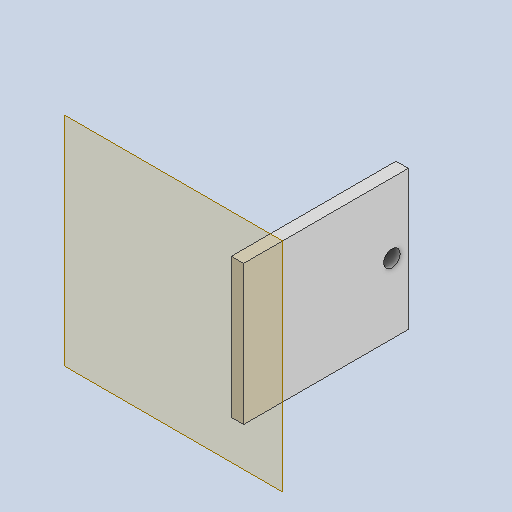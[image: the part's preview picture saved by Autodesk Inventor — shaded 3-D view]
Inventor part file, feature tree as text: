
AUTODESK INVENTOR PART (.ipt)
format: ipt  version: 2022.2 (Build 262287000, 287)  size: 88,576 bytes
history: native  units: in
note: dims shown in document units (in); Inventor stores cm internally (conversion verified against a paired STEP export)
features: other x3, sketch x1, plane x1
ambient origin geometry x8: Origin, YZ Plane, XZ Plane, XY Plane, X Axis, Y Axis, Z Axis, Center Point
bodies: Solid1 (feature_tree)
feature tree (5):
  other  "sideSupportFor12inchBase.ipt"
  other  "Solid1::sideSupportFor12inchBase.ipt"
  other  "TaggingFeature1"
  sketch  "Sketch1"  dims[d0=0.3937in]
  plane  "Work Plane1"
